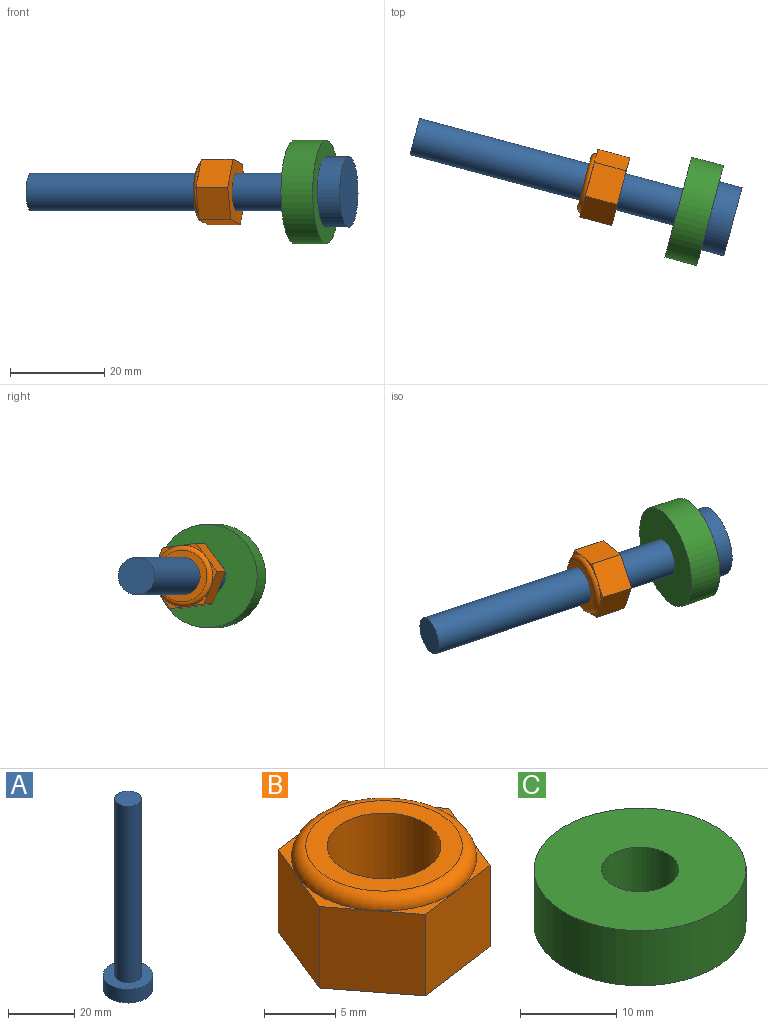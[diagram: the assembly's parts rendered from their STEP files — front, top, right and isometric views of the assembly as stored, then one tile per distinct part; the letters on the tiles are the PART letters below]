
ASSEMBLY  parts=3 mates=2
PART A: 5 faces, bbox 15x15x70 mm
  f0: cylinder r=4mm len=65mm, axis (0,0,-1), area 1633.6mm2, adj f1,f4
  f1: plane 8x8mm, normal (0,0,1), area 50.3mm2, adj f0
  f2: cylinder r=7.5mm len=15mm, axis (0,0,1), area 235.6mm2, adj f3,f4
  f3: plane 15x15mm, normal (0,0,-1), area 176.7mm2, adj f2
  f4: plane 15x15mm, normal (0,0,1), area 126.4mm2, adj f0,f2
PART B: 16 faces, bbox 14.9x14.1x8 mm
  f0: plane 7x6.94mm, normal (-0.92,0.38,0), area 52.5mm2, adj f1,f2,f8,f11,f14
  f1: plane 7x5.94mm, normal (-0.79,-0.61,0), area 52.5mm2, adj f0,f4,f8,f10,f14
  f2: plane 7.44x7mm, normal (-0.13,0.99,0), area 52.5mm2, adj f0,f3,f8,f11,f13
  f3: plane 7x5.94mm, normal (0.79,0.61,0), area 52.5mm2, adj f2,f5,f8,f9,f13
  f4: plane 7.44x7mm, normal (0.13,-0.99,0), area 52.5mm2, adj f1,f5,f8,f10,f12
  f5: plane 7x6.94mm, normal (0.92,-0.38,0), area 52.5mm2, adj f3,f4,f8,f9,f12
  f6: cylinder r=4mm len=8mm, axis (0,0,-1), area 201.1mm2, adj f7,f8
  f7: plane 11x11mm, normal (0,0,1), area 44.8mm2, adj f6,f15
  f8: plane 14.88x13.88mm, normal (0,0,-1), area 96.1mm2, adj f0,f1,f2,f3,f4,f5,f6
  f9: plane 6.44x2.29mm, normal (0,0,1), area 2.3mm2, adj f3,f5,f15
  f10: plane 6.01x2.97mm, normal (0,0,1), area 2.3mm2, adj f1,f4,f15
  f11: plane 5.15x3.97mm, normal (0,0,1), area 2.3mm2, adj f0,f2,f15
  f12: plane 5.15x3.97mm, normal (0,0,1), area 2.3mm2, adj f4,f5,f15
  f13: plane 6.01x2.97mm, normal (0,0,1), area 2.3mm2, adj f2,f3,f15
  f14: plane 6.44x2.29mm, normal (0,0,1), area 2.3mm2, adj f0,f1,f15
  f15: torus R=5.5mm, axis (0,0,1), area 60.6mm2, adj f7,f9,f10,f11,f12,f13,f14
PART C: 4 faces, bbox 22x22x7 mm
  f0: cylinder r=4mm len=8mm, axis (0,0,-1), area 175.9mm2, adj f2,f3
  f1: cylinder r=11mm len=22mm, axis (0,0,-1), area 483.8mm2, adj f2,f3
  f2: plane 22x22mm, normal (0,0,1), area 329.9mm2, adj f0,f1
  f3: plane 22x22mm, normal (0,0,-1), area 329.9mm2, adj f0,f1
PLACE A rot(axis=(-0.13,-0.98,-0.13),91deg) t=(65.43,-38.78,-33.47)mm
PLACE B rot(axis=(-0.68,-0.52,0.52),111.8deg) t=(62.67,27.03,-123.91)mm
PLACE C rot(axis=(-0.68,-0.52,0.52),111.8deg) t=(72.11,-13.84,-95.06)mm
MATE cylindrical B.f6 <-> A.f0  axis (0.97,-0.26,0) through (39.46,-28.66,-91.25)mm
MATE cylindrical C.f0 <-> A.f0  axis (0.97,-0.26,0) through (59.46,-34.02,-91.25)mm
